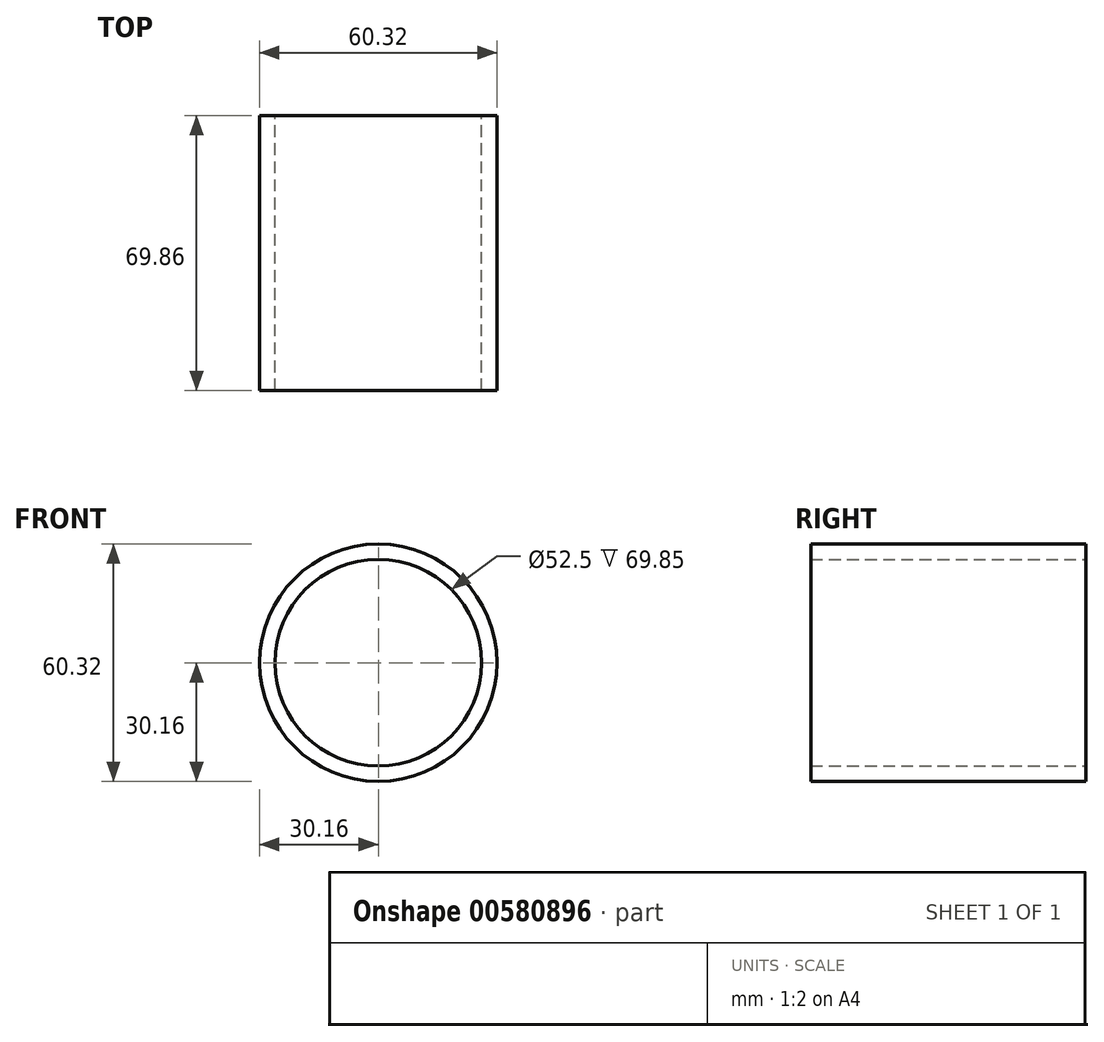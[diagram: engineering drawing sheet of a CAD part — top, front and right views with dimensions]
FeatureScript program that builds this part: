
annotation { "Feature Type Name" : "Feature", "Feature Type Description" : "" }
export const myFeature = defineFeature(function(context is Context, id is Id, definition is map)
    precondition{}
    {
        {
            var Q0;
            Q0=qCreatedBy(makeId("Front.planeOp"),FACE);
            var sketch = newSketch(context, id + "F0", { "sketchPlane" : qUnion([Q0])});
            skCircle(sketch, "E0", {"center": v(0, 0) * mm, "radius": 30.16 * mm});
            skCircle(sketch, "E1.0", {"center": v(0, 0) * mm, "radius": 26.25 * mm});
            skSolve(sketch);
        }
        {
            var Q0;
            Q0 = qSketchRegion(id + "F0", true);
            extrude(context, id + "F1", {"entities" : qUnion([Q0]), "endBound" : BoundingType.SYMMETRIC, "depth" : 69.85 * mm, "offsetDistance" : 25 * mm});
        }
    });
